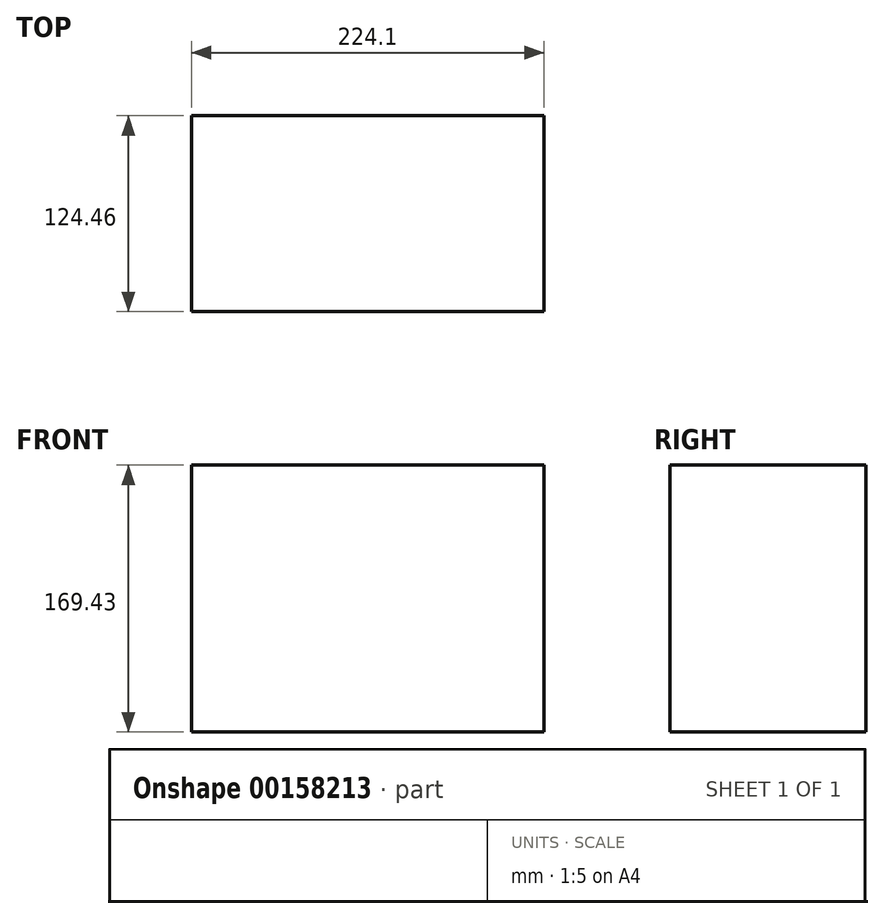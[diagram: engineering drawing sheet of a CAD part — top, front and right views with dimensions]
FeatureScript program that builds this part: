
annotation { "Feature Type Name" : "Feature", "Feature Type Description" : "" }
export const myFeature = defineFeature(function(context is Context, id is Id, definition is map)
    precondition{}
    {
        {
            var Q0;
            Q0=qCreatedBy(makeId("Front.planeOp"),FACE);
            var sketch = newSketch(context, id + "F0", { "sketchPlane" : qUnion([Q0])});
            skLineSegment(sketch, "E0.bottom", {"start": v(-149.64, -74.65) * mm, "end": v(74.46, -74.65) * mm});
            skLineSegment(sketch, "E0.top", {"start": v(-149.64, 94.78) * mm, "end": v(74.46, 94.78) * mm});
            skLineSegment(sketch, "E0.left", {"start": v(-149.64, -74.65) * mm, "end": v(-149.64, 94.78) * mm});
            skLineSegment(sketch, "E0.right", {"start": v(74.46, -74.65) * mm, "end": v(74.46, 94.78) * mm});
            skSolve(sketch);
        }
        {
            var Q0;
            Q0 = qSketchRegion(id + "F0", true);
            extrude(context, id + "F1", {"entities" : qUnion([Q0]), "oppositeDirection" : true, "depth" : 124.46 * mm});
        }
        {
            var Q0;
            Q0=makeQuery(id+"F1.opExtrude","SWEPT_FACE",FACE,{"disambiguationData":[OSD([sQuery(id+"F0.wireOp",EDGE,"E0.top")])]});
            var sketch = newSketch(context, id + "F2", { "sketchPlane" : qUnion([Q0])});
            skCircle(sketch, "E1", {"center": v(-81.75, 68.54) * mm, "radius": 43.21 * mm});
            skSolve(sketch);
        }
        {
            var Q0;
            Q0=sQuery(id+"F2.wireOp",EDGE,"E1");
            extrude(context, id + "F3", {"bodyType" : ToolBodyType.SURFACE, "surfaceEntities" : qUnion([Q0]), "oppositeDirection" : true, "depth" : 300.35 * mm});
        }
        {
            var Q0;
            Q0=makeQuery(id+"F1.opExtrude","SWEPT_FACE",FACE,{"disambiguationData":[OSD([sQuery(id+"F0.wireOp",EDGE,"E0.bottom")])]});
            var sketch = newSketch(context, id + "F4", { "sketchPlane" : qUnion([Q0])});
            skLineSegment(sketch, "E2", {"start": v(-96.06, -171.92) * mm, "end": v(177.38, -148.85) * mm});
            skSolve(sketch);
        }
        {
            var Q0;
            Q0=sQuery(id+"F4.wireOp",EDGE,"E2");
            extrude(context, id + "F5", {"bodyType" : ToolBodyType.SURFACE, "surfaceEntities" : qUnion([Q0]), "depth" : 216.53 * mm});
        }
    });
